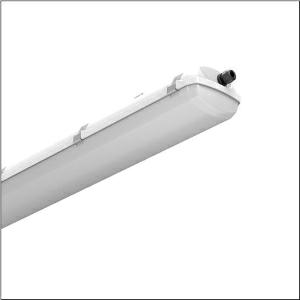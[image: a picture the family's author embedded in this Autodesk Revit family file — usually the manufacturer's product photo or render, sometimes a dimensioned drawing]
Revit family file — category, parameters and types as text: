
# Revit family: monsun_r__ex_51fxa27l460a3g_69c2
name_source: partatom
category: Lighting Fixtures
units: mm (PartAtom-declared; Revit-internal decimal feet)

## family parameters
Cut with Voids When Loaded = No
Host = Face
Light Source = No
Part Type = Normal
Room Calculation Point = No
Round Connector Dimension = Use Diameter
Shared = No

## types (1)
- --- (1 x LED, 6560 lm, 53 W, 4000K)
    Apparent Load = 53 VA
    CIE Flux Codes = 46 76 94 98 100
    Color Rendering = 80
    Color Temperature = 4000K
    Default Elevation = 1800 mm
    Description = Monsun® Ex, damp-proof luminaire, primary optical cover: cover, of PC, UV-stabilised, opal, light emission: direct distribution, primary light characteristic: symmetric, installation type: surface-mounted, LED, rated luminous flux: 6.560lm, luminous efficacy: 124lm/W, light colour: 840, colour temperature: 4000K, control gear: ECG, with terminal, 3+1-pole, max. 2.5mm², through-wiring: 6x 2.5mm², mains connection: 220..250V, AC, 50/60Hz, rated input power: 53W, control gear: single battery element, housing, of PC, light grey (RAL 7035), incl. 1x Ex cable gland M20 for cable diameter 7..12mm with sealing, incl. 1x Ex locking screw M20 with sealing, length: 1.280mm, width: 155mm, height: 105mm, clip for enclosure, of stainless steel, protection rating (complete): IP66, insulation class (complete): insulation class I (protective earthing), certification: CE, explosion class: zone 1,21 II 2G Ex eb mb op is IIC T4 Gb, II 2D Ex tb op is IIIC T67°C Db, impact resistance: IK10, permissible operating ambient temperature: 0..+35°C, contact your sales advisor before using the luminaires in applications with unclear chemical exposure, large temperature fluctuations or condensation-forming humidity, packaging unit: 1 piece
    Height = 105 mm
    Lamp = 1 x LED
    Lamp Light Flux = 6560 lm
    Lamp Power = 53 W
    Lamp count = 1
    Length = 1280 mm
    Luminous efficacy = 124 lm/W
    Manufacturer = Siteco
    ModVariant = No
    Model = 51FXA27L460A3G
    Mounting Place = Ceiling
    Mounting Type = Surface mounted
    Number of Poles = 1
    OnlyDefault = Yes
    Power Factor = 1
    Product Name = Monsun® Ex
    Product group = damp-proof luminaire
    ProductGroupID = 301
    Protection Class = Protection class I
    Protection Degree = IP 66
    RLX_Detail_Level = 1
    RLX_Emergency_Light_Flux = 0 lm
    RLX_Emergency_Type = 0
    RLX_Emergency_Type_DB = No
    RlxData = <blob elided: 41853 chars, md5=5e038989>
    Socket = socket
    Standby Power = 0 W
    System Light Flux = 6560 lm
    System Power = 53 W
    Type Comments = -
    Type Image = l_1258882.jpg
    URL = http://relux.com
    VarID = @adj_022345
    Voltage = 0 V
    Weight = 0.00 kg
    Width = 155 mm

## geometry (parser evidence)
native form markers: Blend x4, Sweep x8
no freeform markers — native parametric forms only
